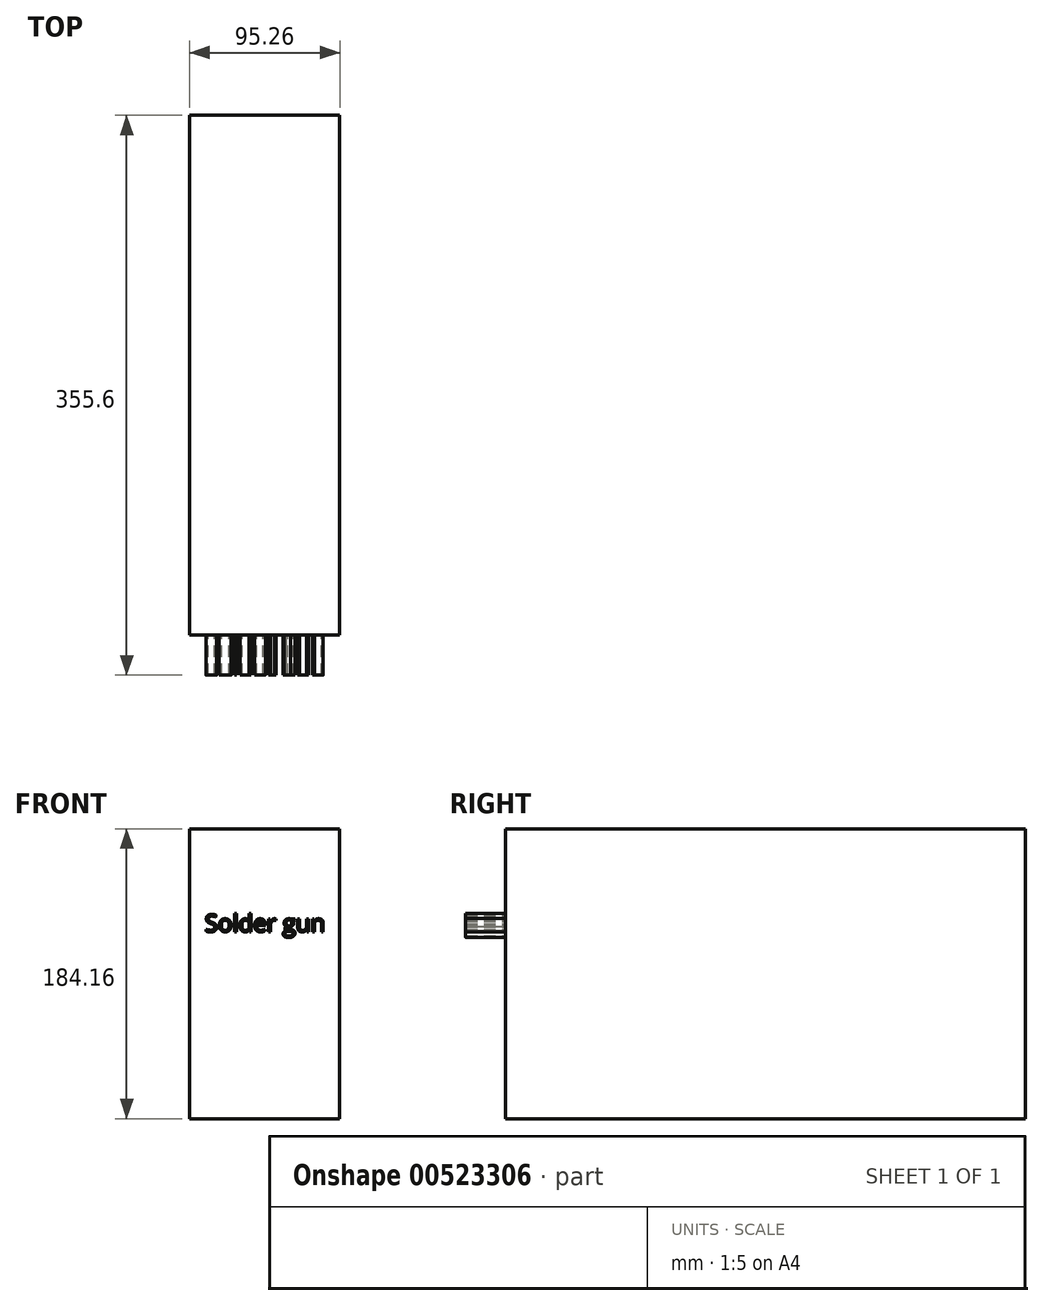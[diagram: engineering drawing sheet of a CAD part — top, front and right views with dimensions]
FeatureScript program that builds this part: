
annotation { "Feature Type Name" : "Feature", "Feature Type Description" : "" }
export const myFeature = defineFeature(function(context is Context, id is Id, definition is map)
    precondition{}
    {
        {
            var Q0;
            Q0=qCreatedBy(makeId("Front.planeOp"),FACE);
            var sketch = newSketch(context, id + "F0", { "sketchPlane" : qUnion([Q0])});
            skLineSegment(sketch, "E0.bottom", {"start": v(47.62, 92.08) * mm, "end": v(-47.63, 92.08) * mm});
            skLineSegment(sketch, "E0.top", {"start": v(47.62, -92.08) * mm, "end": v(-47.62, -92.08) * mm});
            skLineSegment(sketch, "E0.left", {"start": v(47.62, 92.08) * mm, "end": v(47.62, -92.08) * mm});
            skLineSegment(sketch, "E0.right", {"start": v(-47.63, 92.08) * mm, "end": v(-47.62, -92.08) * mm});
            skPoint(sketch, "E0.middle", {"position": v(0, 0) * mm});
            skSolve(sketch);
        }
        {
            var Q0;
            Q0=makeQuery(id+"F0.imprint","IMPRINT",FACE,{"disambiguationData":[TD([[makeQuery(id+"F0.imprint","IMPRINT",EDGE,{"derivedFrom":sQuery(id+"F0.wireOp",EDGE,"E0.bottom")}),1.0]])]});
            extrude(context, id + "F1", {"entities" : qUnion([Q0]), "depth" : 330.2 * mm, "offsetDistance" : 25.4 * mm});
        }
        {
            var Q0;
            Q0=makeQuery(id+"F1.opExtrude","CAP_FACE",FACE,{"disambiguationData":[OSD([sQuery(id+"F0.wireOp",EDGE,"E0.bottom"),sQuery(id+"F0.wireOp",EDGE,"E0.top"),sQuery(id+"F0.wireOp",EDGE,"E0.left"),sQuery(id+"F0.wireOp",EDGE,"E0.right")])],"isStart":false});
            var sketch = newSketch(context, id + "F2", { "sketchPlane" : qUnion([Q0])});
            skText(sketch, "E1", { "text": "Solder gun", "fontName": "OpenSans-Regular.ttf"});
            const initialGuessF2  = {"E1": [-0.0381, 0.02667, 1, 0, 0.01096]};
            skSetInitialGuess(sketch, initialGuessF2);
            skSolve(sketch);
        }
        {
            var Q0;
            Q0 = qSketchRegion(id + "F2", true);
            extrude(context, id + "F3", {"entities" : qUnion([Q0]), "operationType" : NewBodyOperationType.ADD, "depth" : 25.4 * mm, "offsetDistance" : 25.4 * mm});
        }
    });
